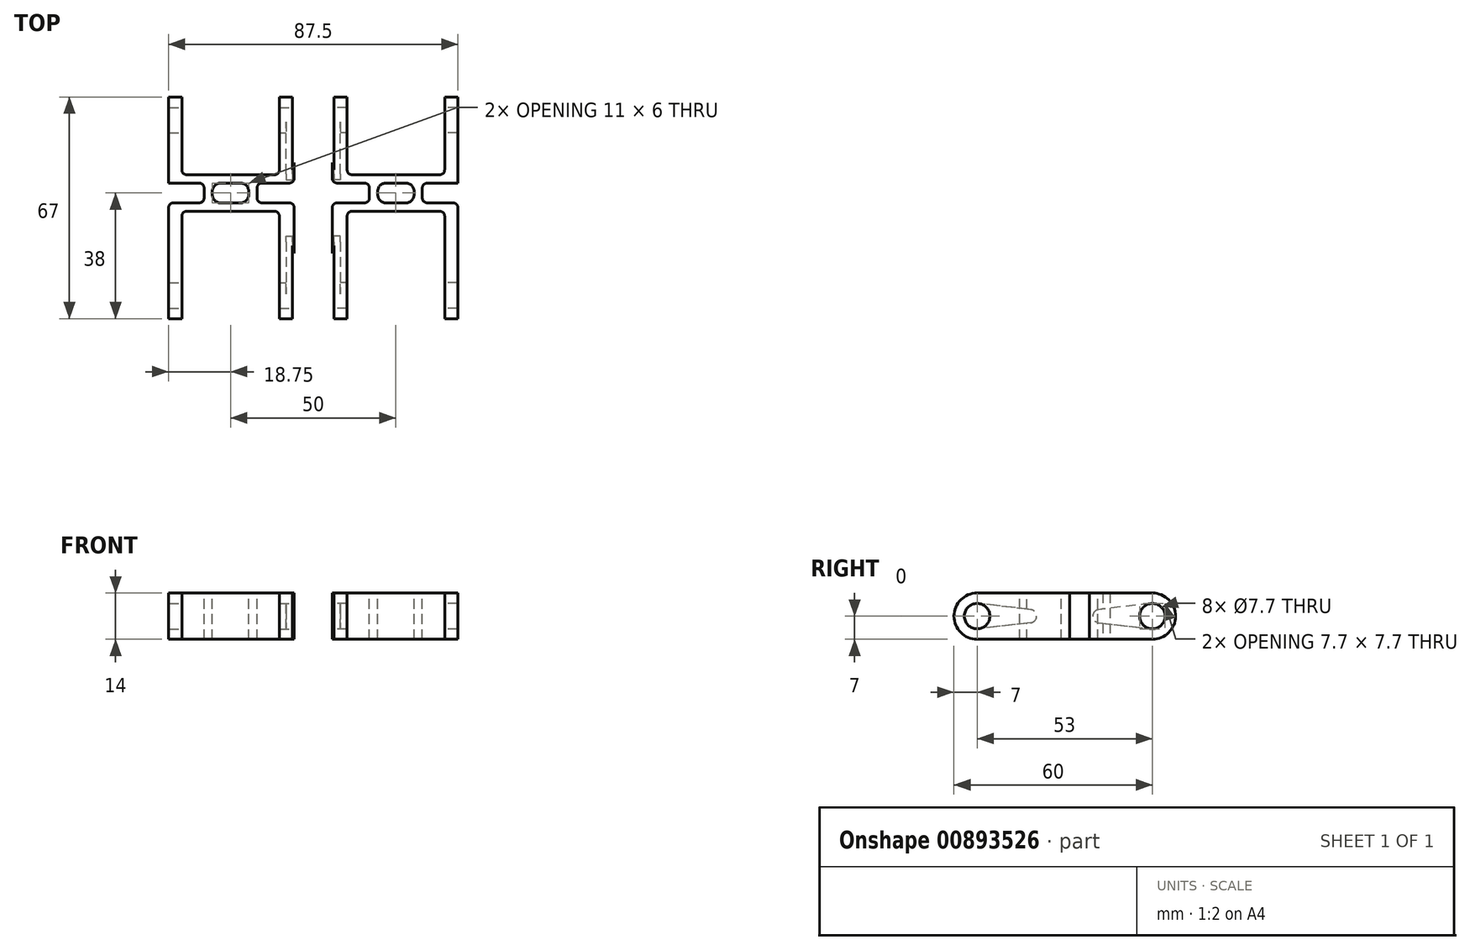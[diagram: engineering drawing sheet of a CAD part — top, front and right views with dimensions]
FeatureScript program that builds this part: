
annotation { "Feature Type Name" : "Feature", "Feature Type Description" : "" }
export const myFeature = defineFeature(function(context is Context, id is Id, definition is map)
    precondition{}
    {
        {
            var Q0;
            Q0=qCreatedBy(makeId("Top.planeOp"),FACE);
            var sketch = newSketch(context, id + "F0", { "sketchPlane" : qUnion([Q0])});
            skLineSegment(sketch, "E0.bottom", {"start": v(18.75, 33.5) * mm, "end": v(-18.75, 33.5) * mm});
            skLineSegment(sketch, "E0.top", {"start": v(18.75, -33.5) * mm, "end": v(-18.75, -33.5) * mm});
            skLineSegment(sketch, "E0.left", {"start": v(18.75, 33.5) * mm, "end": v(18.75, -33.5) * mm});
            skLineSegment(sketch, "E0.right", {"start": v(-18.75, 33.5) * mm, "end": v(-18.75, -33.5) * mm});
            skPoint(sketch, "E0.middle", {"position": v(0, 0) * mm});
            skSolve(sketch);
        }
        {
            var Q0;
            Q0 = qSketchRegion(id + "F0", true);
            extrude(context, id + "F1", {"entities" : qUnion([Q0]), "depth" : 14 * mm, "offsetDistance" : 25 * mm});
        }
        {
            var Q0;
            Q0=makeQuery(id+"F1.opExtrude","CAP_FACE",FACE,{"disambiguationData":[OSD([sQuery(id+"F0.wireOp",EDGE,"E0.bottom"),sQuery(id+"F0.wireOp",EDGE,"E0.top"),sQuery(id+"F0.wireOp",EDGE,"E0.left"),sQuery(id+"F0.wireOp",EDGE,"E0.right")])],"isStart":false});
            var sketch = newSketch(context, id + "F2", { "sketchPlane" : qUnion([Q0])});
            skLineSegment(sketch, "E1.bottom", {"start": v(-18.75, 7.5) * mm, "end": v(-8, 7.5) * mm});
            skLineSegment(sketch, "E1.top", {"start": v(-18.75, 1.5) * mm, "end": v(-8, 1.5) * mm});
            skLineSegment(sketch, "E1.left", {"start": v(-18.75, 7.5) * mm, "end": v(-18.75, 1.5) * mm});
            skLineSegment(sketch, "E1.right", {"start": v(-8, 7.5) * mm, "end": v(-8, 1.5) * mm});
            skLineSegment(sketch, "E2.bottom", {"start": v(18.75, 7.5) * mm, "end": v(8, 7.5) * mm});
            skLineSegment(sketch, "E2.top", {"start": v(18.75, 1.5) * mm, "end": v(8, 1.5) * mm});
            skLineSegment(sketch, "E2.left", {"start": v(18.75, 7.5) * mm, "end": v(18.75, 1.5) * mm});
            skLineSegment(sketch, "E2.right", {"start": v(8, 7.5) * mm, "end": v(8, 1.5) * mm});
            skLineSegment(sketch, "E3.bottom", {"start": v(-14.75, 33.5) * mm, "end": v(14.75, 33.5) * mm});
            skLineSegment(sketch, "E3.top", {"start": v(-14.75, 10) * mm, "end": v(14.75, 10) * mm});
            skLineSegment(sketch, "E3.left", {"start": v(-14.75, 33.5) * mm, "end": v(-14.75, 10) * mm});
            skLineSegment(sketch, "E3.right", {"start": v(14.75, 33.5) * mm, "end": v(14.75, 10) * mm});
            skLineSegment(sketch, "E4.bottom", {"start": v(14.75, -33.5) * mm, "end": v(-14.75, -33.5) * mm});
            skLineSegment(sketch, "E4.top", {"start": v(14.75, -1) * mm, "end": v(-14.75, -1) * mm});
            skLineSegment(sketch, "E4.left", {"start": v(14.75, -33.5) * mm, "end": v(14.75, -1) * mm});
            skLineSegment(sketch, "E4.right", {"start": v(-14.75, -33.5) * mm, "end": v(-14.75, -1) * mm});
            skLineSegment(sketch, "E5", {"start": v(-14.75, 33.5) * mm, "end": v(-18.75, 33.5) * mm, "construction": true});
            skLineSegment(sketch, "E6", {"start": v(14.75, 33.5) * mm, "end": v(18.75, 33.5) * mm, "construction": true});
            skLineSegment(sketch, "E7", {"start": v(18.75, -33.5) * mm, "end": v(14.75, -33.5) * mm, "construction": true});
            skLineSegment(sketch, "E8", {"start": v(-14.75, -33.5) * mm, "end": v(-18.75, -33.5) * mm, "construction": true});
            skSolve(sketch);
        }
        {
            var Q0;
            Q0 = qSketchRegion(id + "F2", true);
            extrude(context, id + "F3", {"entities" : qUnion([Q0]), "operationType" : NewBodyOperationType.REMOVE, "oppositeDirection" : true, "depth" : 25 * mm, "offsetDistance" : 25 * mm});
        }
        {
            var Q0;
            {var subQ0=sQuery(id+"F0.wireOp",EDGE,"E0.right");var subQ1=sQuery(id+"F0.wireOp",EDGE,"E0.top");Q0=makeQuery(id+"F3.boolean.opBoolean","SPLIT",EDGE,{"disambiguationData":[TD([makeQuery(id+"F1.opExtrude","SWEPT_FACE",FACE,{"disambiguationData":[OSD([subQ0])]})])],"derivedFrom":makeQuery(id+"F1.opExtrude","CAP_EDGE",EDGE,{"disambiguationData":[OSD([subQ1])],"isStart":false})});}
            var Q1;
            {var subQ0=sQuery(id+"F0.wireOp",EDGE,"E0.right");var subQ1=sQuery(id+"F0.wireOp",EDGE,"E0.top");Q1=makeQuery(id+"F3.boolean.opBoolean","SPLIT",EDGE,{"disambiguationData":[TD([makeQuery(id+"F1.opExtrude","SWEPT_FACE",FACE,{"disambiguationData":[OSD([subQ0])]})])],"derivedFrom":makeQuery(id+"F1.opExtrude","CAP_EDGE",EDGE,{"disambiguationData":[OSD([subQ1])],"isStart":true})});}
            var Q2;
            {var subQ0=sQuery(id+"F0.wireOp",EDGE,"E0.left");var subQ1=sQuery(id+"F0.wireOp",EDGE,"E0.top");Q2=makeQuery(id+"F3.boolean.opBoolean","SPLIT",EDGE,{"disambiguationData":[TD([makeQuery(id+"F1.opExtrude","SWEPT_FACE",FACE,{"disambiguationData":[OSD([subQ0])]})])],"derivedFrom":makeQuery(id+"F1.opExtrude","CAP_EDGE",EDGE,{"disambiguationData":[OSD([subQ1])],"isStart":false})});}
            var Q3;
            {var subQ0=sQuery(id+"F0.wireOp",EDGE,"E0.left");var subQ1=sQuery(id+"F0.wireOp",EDGE,"E0.top");Q3=makeQuery(id+"F3.boolean.opBoolean","SPLIT",EDGE,{"disambiguationData":[TD([makeQuery(id+"F1.opExtrude","SWEPT_FACE",FACE,{"disambiguationData":[OSD([subQ0])]})])],"derivedFrom":makeQuery(id+"F1.opExtrude","CAP_EDGE",EDGE,{"disambiguationData":[OSD([subQ1])],"isStart":true})});}
            var Q4;
            {var subQ0=sQuery(id+"F0.wireOp",EDGE,"E0.bottom");var subQ1=sQuery(id+"F0.wireOp",EDGE,"E0.right");Q4=makeQuery(id+"F3.boolean.opBoolean","SPLIT",EDGE,{"disambiguationData":[TD([makeQuery(id+"F1.opExtrude","SWEPT_FACE",FACE,{"disambiguationData":[OSD([subQ1])]})])],"derivedFrom":makeQuery(id+"F1.opExtrude","CAP_EDGE",EDGE,{"disambiguationData":[OSD([subQ0])],"isStart":false})});}
            var Q5;
            {var subQ0=sQuery(id+"F0.wireOp",EDGE,"E0.bottom");var subQ1=sQuery(id+"F0.wireOp",EDGE,"E0.left");Q5=makeQuery(id+"F3.boolean.opBoolean","SPLIT",EDGE,{"disambiguationData":[TD([makeQuery(id+"F1.opExtrude","SWEPT_FACE",FACE,{"disambiguationData":[OSD([subQ1])]})])],"derivedFrom":makeQuery(id+"F1.opExtrude","CAP_EDGE",EDGE,{"disambiguationData":[OSD([subQ0])],"isStart":false})});}
            var Q6;
            {var subQ0=sQuery(id+"F0.wireOp",EDGE,"E0.bottom");var subQ1=sQuery(id+"F0.wireOp",EDGE,"E0.right");Q6=makeQuery(id+"F3.boolean.opBoolean","SPLIT",EDGE,{"disambiguationData":[TD([makeQuery(id+"F1.opExtrude","SWEPT_FACE",FACE,{"disambiguationData":[OSD([subQ1])]})])],"derivedFrom":makeQuery(id+"F1.opExtrude","CAP_EDGE",EDGE,{"disambiguationData":[OSD([subQ0])],"isStart":true})});}
            var Q7;
            {var subQ0=sQuery(id+"F0.wireOp",EDGE,"E0.bottom");var subQ1=sQuery(id+"F0.wireOp",EDGE,"E0.left");Q7=makeQuery(id+"F3.boolean.opBoolean","SPLIT",EDGE,{"disambiguationData":[TD([makeQuery(id+"F1.opExtrude","SWEPT_FACE",FACE,{"disambiguationData":[OSD([subQ1])]})])],"derivedFrom":makeQuery(id+"F1.opExtrude","CAP_EDGE",EDGE,{"disambiguationData":[OSD([subQ0])],"isStart":true})});}
            fillet(context, id + "F4", {"entities" : qUnion([Q0, Q1, Q2, Q3, Q4, Q5, Q6, Q7]), "radius" : 7 * mm, "tangentPropagation" : true, "defaultsChanged" : true, "vertexSettings" : [], "allowEdgeOverflow" : false});
        }
        {
            var Q0;
            {var subQ1=sQuery(id+"F0.wireOp",EDGE,"E0.left");var subQ2=sQuery(id+"F0.wireOp",EDGE,"E0.top");Q0=makeQuery(id+"F3.boolean.opBoolean","SPLIT",FACE,{"disambiguationData":[TD([makeQuery(id+"F1.opExtrude","SWEPT_FACE",FACE,{"disambiguationData":[OSD([subQ2])]})])],"derivedFrom":makeQuery(id+"F1.opExtrude","SWEPT_FACE",FACE,{"disambiguationData":[OSD([subQ1])]})});}
            var sketch = newSketch(context, id + "F5", { "sketchPlane" : qUnion([Q0])});
            skCircle(sketch, "E9", {"center": v(-26.5, 7) * mm, "radius": 3.85 * mm});
            skCircle(sketch, "E10", {"center": v(26.5, 7) * mm, "radius": 3.85 * mm});
            skSolve(sketch);
        }
        {
            var Q0;
            Q0 = qSketchRegion(id + "F5", true);
            extrude(context, id + "F6", {"entities" : qUnion([Q0]), "operationType" : NewBodyOperationType.REMOVE, "endBound" : BoundingType.THROUGH_ALL, "oppositeDirection" : true, "depth" : 25 * mm, "offsetDistance" : 25 * mm});
        }
        {
            var Q0;
            {var subQ1=sQuery(id+"F0.wireOp",EDGE,"E0.left");var subQ2=sQuery(id+"F0.wireOp",EDGE,"E0.top");Q0=makeQuery(id+"F3.boolean.opBoolean","SPLIT",FACE,{"disambiguationData":[TD([makeQuery(id+"F1.opExtrude","SWEPT_FACE",FACE,{"disambiguationData":[OSD([subQ2])]})])],"derivedFrom":makeQuery(id+"F1.opExtrude","SWEPT_FACE",FACE,{"disambiguationData":[OSD([subQ1])]})});}
            var sketch = newSketch(context, id + "F7", { "sketchPlane" : qUnion([Q0])});
            skLineSegment(sketch, "E11", {"start": v(-26.5, 7) * mm, "end": v(-10.5, 7) * mm, "construction": true});
            skCircle(sketch, "E12", {"center": v(-10.5, 7) * mm, "radius": 2 * mm});
            skLineSegment(sketch, "E13", {"start": v(26.5, 7) * mm, "end": v(10.5, 7) * mm, "construction": true});
            skCircle(sketch, "E14", {"center": v(10.5, 7) * mm, "radius": 2 * mm});
            skCircle(sketch, "E15.0", {"center": v(-26.5, 7) * mm, "radius": 3.85 * mm});
            skCircle(sketch, "E15.1", {"center": v(26.5, 7) * mm, "radius": 3.85 * mm});
            skLineSegment(sketch, "E16", {"start": v(26.05, 10.82) * mm, "end": v(10.27, 8.99) * mm});
            skLineSegment(sketch, "E17", {"start": v(10.27, 5.01) * mm, "end": v(26.05, 3.18) * mm});
            skLineSegment(sketch, "E18", {"start": v(-10.27, 8.99) * mm, "end": v(-26.05, 10.82) * mm});
            skLineSegment(sketch, "E19", {"start": v(-10.27, 5.01) * mm, "end": v(-26.05, 3.18) * mm});
            skSolve(sketch);
        }
        {
            var Q0;
            {var subQ0=sQuery(id+"F7.wireOp",EDGE,"E18");Q0=makeQuery(id+"F7.imprint","IMPRINT",FACE,{"disambiguationData":[TD([[makeQuery(id+"F7.imprint","IMPRINT",EDGE,{"derivedFrom":subQ0}),1.0]])]});}
            var Q1;
            {var subQ0=sQuery(id+"F7.wireOp",EDGE,"E12");var subQ1=makeQuery(id+"F7.imprint","INTERSECT",VERTEX,{"derivedFrom":[subQ0,sQuery(id+"F7.wireOp",EDGE,"E18")]});Q1=makeQuery(id+"F7.imprint","IMPRINT",FACE,{"disambiguationData":[TD([[makeQuery(id+"F7.imprint","IMPRINT",EDGE,{"disambiguationData":[TD([[subQ1,-1.0]])],"derivedFrom":subQ0}),1.0]])]});}
            var Q2;
            {var subQ0=sQuery(id+"F7.wireOp",EDGE,"E14");var subQ1=makeQuery(id+"F7.imprint","INTERSECT",VERTEX,{"derivedFrom":[subQ0,sQuery(id+"F7.wireOp",EDGE,"E16")]});Q2=makeQuery(id+"F7.imprint","IMPRINT",FACE,{"disambiguationData":[TD([[makeQuery(id+"F7.imprint","IMPRINT",EDGE,{"disambiguationData":[TD([[subQ1,-1.0]])],"derivedFrom":subQ0}),1.0]])]});}
            var Q3;
            {var subQ0=sQuery(id+"F7.wireOp",EDGE,"E16");Q3=makeQuery(id+"F7.imprint","IMPRINT",FACE,{"disambiguationData":[TD([[makeQuery(id+"F7.imprint","IMPRINT",EDGE,{"derivedFrom":subQ0}),1.0]])]});}
            extrude(context, id + "F8", {"entities" : qUnion([Q0, Q1, Q2, Q3]), "operationType" : NewBodyOperationType.REMOVE, "oppositeDirection" : true, "depth" : 1.9 * mm, "offsetDistance" : 25 * mm});
        }
        {
            var Q0;
            Q0=qCreatedBy(makeId("Right.planeOp"),FACE);
            cPlane(context, id + "F9", {"entities" : qUnion([Q0]), "cplaneType" : CPlaneType.OFFSET, "offset" : 25 * mm, "width" : 150 * mm, "height" : 150 * mm});
        }
        {
            var Q0;
            Q0=makeQuery(id+"F1.opExtrude","SWEPT_BODY",BODY,{"disambiguationData":[OSD([sQuery(id+"F0.wireOp",EDGE,"E0.bottom"),sQuery(id+"F0.wireOp",EDGE,"E0.top"),sQuery(id+"F0.wireOp",EDGE,"E0.left"),sQuery(id+"F0.wireOp",EDGE,"E0.right")])]});
            var Q1;
            Q1=qCreatedBy(id+"F9.planeOp",FACE);
            mirror(context, id + "F10", {"entities" : qUnion([Q0]), "mirrorPlane" : qUnion([Q1])});
        }
        {
            var Q0;
            {var subQ1=sQuery(id+"F0.wireOp",EDGE,"E0.left");var subQ2=sQuery(id+"F0.wireOp",EDGE,"E0.top");Q0=makeQuery(id+"F3.boolean.opBoolean","SPLIT",FACE,{"disambiguationData":[TD([makeQuery(id+"F1.opExtrude","SWEPT_FACE",FACE,{"disambiguationData":[OSD([subQ2])]})])],"derivedFrom":makeQuery(id+"F1.opExtrude","SWEPT_FACE",FACE,{"disambiguationData":[OSD([subQ1])]})});}
            var Q1;
            {var subQ1=sQuery(id+"F0.wireOp",EDGE,"E0.left");var subQ2=sQuery(id+"F0.wireOp",EDGE,"E0.top");Q1=makeQuery(id+"F3.boolean.opBoolean","SPLIT",FACE,{"disambiguationData":[TD([makeQuery(id+"F1.opExtrude","SWEPT_FACE",FACE,{"disambiguationData":[OSD([subQ2])]})])],"derivedFrom":makeQuery(id+"F1.opExtrude","SWEPT_FACE",FACE,{"disambiguationData":[OSD([subQ1])]})});}
            var sketch = newSketch(context, id + "F11", { "sketchPlane" : qUnion([Q0, Q1])});
            skLineSegment(sketch, "E20.bottom", {"start": v(-16.5, 14) * mm, "end": v(1.5, 14) * mm});
            skLineSegment(sketch, "E20.top", {"start": v(-16.5, 0) * mm, "end": v(1.5, 0) * mm});
            skLineSegment(sketch, "E20.left", {"start": v(-16.5, 14) * mm, "end": v(-16.5, 0) * mm});
            skLineSegment(sketch, "E20.right", {"start": v(1.5, 14) * mm, "end": v(1.5, 0) * mm});
            skLineSegment(sketch, "E21.bottom", {"start": v(7.5, 0) * mm, "end": v(16.5, 0) * mm});
            skLineSegment(sketch, "E21.top", {"start": v(7.5, 14) * mm, "end": v(16.5, 14) * mm});
            skLineSegment(sketch, "E21.left", {"start": v(7.5, 0) * mm, "end": v(7.5, 14) * mm});
            skLineSegment(sketch, "E21.right", {"start": v(16.5, 0) * mm, "end": v(16.5, 14) * mm});
            skSolve(sketch);
        }
        {
            var Q0;
            Q0 = qSketchRegion(id + "F11", true);
            extrude(context, id + "F12", {"entities" : qUnion([Q0]), "operationType" : NewBodyOperationType.ADD, "depth" : 0.5 * mm, "offsetDistance" : 25 * mm});
        }
        {
            var Q0;
            {var subQ1=sQuery(id+"F0.wireOp",EDGE,"E0.left");var subQ2=sQuery(id+"F0.wireOp",EDGE,"E0.top");Q0=makeQuery(id+"F10.opPattern","COPY",FACE,{"derivedFrom":makeQuery(id+"F3.boolean.opBoolean","SPLIT",FACE,{"disambiguationData":[TD([makeQuery(id+"F1.opExtrude","SWEPT_FACE",FACE,{"disambiguationData":[OSD([subQ2])]})])],"derivedFrom":makeQuery(id+"F1.opExtrude","SWEPT_FACE",FACE,{"disambiguationData":[OSD([subQ1])]})}),"instanceName":"1"});}
            var sketch = newSketch(context, id + "F13", { "sketchPlane" : qUnion([Q0])});
            skLineSegment(sketch, "E22.bottom", {"start": v(-1.5, 14) * mm, "end": v(16.5, 14) * mm});
            skLineSegment(sketch, "E22.top", {"start": v(-1.5, 0) * mm, "end": v(16.5, 0) * mm});
            skLineSegment(sketch, "E22.left", {"start": v(-1.5, 14) * mm, "end": v(-1.5, 0) * mm});
            skLineSegment(sketch, "E22.right", {"start": v(16.5, 14) * mm, "end": v(16.5, 0) * mm});
            skLineSegment(sketch, "E23.bottom", {"start": v(-7.5, 14) * mm, "end": v(-16.5, 14) * mm});
            skLineSegment(sketch, "E23.top", {"start": v(-7.5, 0) * mm, "end": v(-16.5, 0) * mm});
            skLineSegment(sketch, "E23.left", {"start": v(-7.5, 14) * mm, "end": v(-7.5, 0) * mm});
            skLineSegment(sketch, "E23.right", {"start": v(-16.5, 14) * mm, "end": v(-16.5, 0) * mm});
            skSolve(sketch);
        }
        {
            var Q0;
            Q0 = qSketchRegion(id + "F13", true);
            extrude(context, id + "F14", {"entities" : qUnion([Q0]), "operationType" : NewBodyOperationType.ADD, "depth" : 0.5 * mm, "offsetDistance" : 25 * mm});
        }
        {
            var Q0;
            Q0=makeQuery(id+"F12.opExtrude","CAP_EDGE",EDGE,{"disambiguationData":[OSD([sQuery(id+"F11.wireOp",EDGE,"E20.right")])],"isStart":false});
            var Q1;
            Q1=makeQuery(id+"F12.opExtrude","CAP_EDGE",EDGE,{"disambiguationData":[OSD([sQuery(id+"F11.wireOp",EDGE,"E21.left")])],"isStart":false});
            var Q2;
            Q2=makeQuery(id+"F3.boolean.opBoolean","COPY",EDGE,{"derivedFrom":makeQuery(id+"F3.opExtrude","SWEPT_EDGE",EDGE,{"disambiguationData":[OSD([sQuery(id+"F2.wireOp",EDGE,"E2.bottom"),sQuery(id+"F2.wireOp",EDGE,"E2.right")])]})});
            var Q3;
            Q3=makeQuery(id+"F3.boolean.opBoolean","COPY",EDGE,{"derivedFrom":makeQuery(id+"F3.opExtrude","SWEPT_EDGE",EDGE,{"disambiguationData":[OSD([sQuery(id+"F2.wireOp",EDGE,"E2.top"),sQuery(id+"F2.wireOp",EDGE,"E2.right")])]})});
            var Q4;
            Q4=makeQuery(id+"F3.boolean.opBoolean","COPY",EDGE,{"derivedFrom":makeQuery(id+"F3.opExtrude","SWEPT_EDGE",EDGE,{"disambiguationData":[OSD([sQuery(id+"F0.wireOp",EDGE,"E0.right"),sQuery(id+"F2.wireOp",EDGE,"E1.bottom"),sQuery(id+"F2.wireOp",EDGE,"E1.left")])]})});
            var Q5;
            Q5=makeQuery(id+"F3.boolean.opBoolean","COPY",EDGE,{"derivedFrom":makeQuery(id+"F3.opExtrude","SWEPT_EDGE",EDGE,{"disambiguationData":[OSD([sQuery(id+"F0.wireOp",EDGE,"E0.right"),sQuery(id+"F2.wireOp",EDGE,"E1.top"),sQuery(id+"F2.wireOp",EDGE,"E1.left")])]})});
            var Q6;
            Q6=makeQuery(id+"F3.boolean.opBoolean","COPY",EDGE,{"derivedFrom":makeQuery(id+"F3.opExtrude","SWEPT_EDGE",EDGE,{"disambiguationData":[OSD([sQuery(id+"F2.wireOp",EDGE,"E1.bottom"),sQuery(id+"F2.wireOp",EDGE,"E1.right")])]})});
            var Q7;
            Q7=makeQuery(id+"F3.boolean.opBoolean","COPY",EDGE,{"derivedFrom":makeQuery(id+"F3.opExtrude","SWEPT_EDGE",EDGE,{"disambiguationData":[OSD([sQuery(id+"F2.wireOp",EDGE,"E1.top"),sQuery(id+"F2.wireOp",EDGE,"E1.right")])]})});
            var Q8;
            Q8=makeQuery(id+"F3.boolean.opBoolean","COPY",EDGE,{"derivedFrom":makeQuery(id+"F3.opExtrude","SWEPT_EDGE",EDGE,{"disambiguationData":[OSD([sQuery(id+"F2.wireOp",EDGE,"E4.top"),sQuery(id+"F2.wireOp",EDGE,"E4.right")])]})});
            var Q9;
            Q9=makeQuery(id+"F3.boolean.opBoolean","COPY",EDGE,{"derivedFrom":makeQuery(id+"F3.opExtrude","SWEPT_EDGE",EDGE,{"disambiguationData":[OSD([sQuery(id+"F2.wireOp",EDGE,"E4.top"),sQuery(id+"F2.wireOp",EDGE,"E4.left")])]})});
            var Q10;
            Q10=makeQuery(id+"F3.boolean.opBoolean","COPY",EDGE,{"derivedFrom":makeQuery(id+"F3.opExtrude","SWEPT_EDGE",EDGE,{"disambiguationData":[OSD([sQuery(id+"F2.wireOp",EDGE,"E3.top"),sQuery(id+"F2.wireOp",EDGE,"E3.left")])]})});
            var Q11;
            Q11=makeQuery(id+"F3.boolean.opBoolean","COPY",EDGE,{"derivedFrom":makeQuery(id+"F3.opExtrude","SWEPT_EDGE",EDGE,{"disambiguationData":[OSD([sQuery(id+"F2.wireOp",EDGE,"E3.top"),sQuery(id+"F2.wireOp",EDGE,"E3.right")])]})});
            var Q12;
            Q12=makeQuery(id+"F14.opExtrude","CAP_EDGE",EDGE,{"disambiguationData":[OSD([sQuery(id+"F13.wireOp",EDGE,"E23.left")])],"isStart":false});
            var Q13;
            Q13=makeQuery(id+"F14.opExtrude","CAP_EDGE",EDGE,{"disambiguationData":[OSD([sQuery(id+"F13.wireOp",EDGE,"E22.left")])],"isStart":false});
            var Q14;
            Q14=makeQuery(id+"F10.opPattern","COPY",EDGE,{"derivedFrom":makeQuery(id+"F3.boolean.opBoolean","COPY",EDGE,{"derivedFrom":makeQuery(id+"F3.opExtrude","SWEPT_EDGE",EDGE,{"disambiguationData":[OSD([sQuery(id+"F2.wireOp",EDGE,"E2.top"),sQuery(id+"F2.wireOp",EDGE,"E2.right")])]})}),"instanceName":"1"});
            var Q15;
            Q15=makeQuery(id+"F10.opPattern","COPY",EDGE,{"derivedFrom":makeQuery(id+"F3.boolean.opBoolean","COPY",EDGE,{"derivedFrom":makeQuery(id+"F3.opExtrude","SWEPT_EDGE",EDGE,{"disambiguationData":[OSD([sQuery(id+"F2.wireOp",EDGE,"E2.bottom"),sQuery(id+"F2.wireOp",EDGE,"E2.right")])]})}),"instanceName":"1"});
            var Q16;
            Q16=makeQuery(id+"F10.opPattern","COPY",EDGE,{"derivedFrom":makeQuery(id+"F3.boolean.opBoolean","COPY",EDGE,{"derivedFrom":makeQuery(id+"F3.opExtrude","SWEPT_EDGE",EDGE,{"disambiguationData":[OSD([sQuery(id+"F2.wireOp",EDGE,"E1.bottom"),sQuery(id+"F2.wireOp",EDGE,"E1.right")])]})}),"instanceName":"1"});
            var Q17;
            Q17=makeQuery(id+"F10.opPattern","COPY",EDGE,{"derivedFrom":makeQuery(id+"F3.boolean.opBoolean","COPY",EDGE,{"derivedFrom":makeQuery(id+"F3.opExtrude","SWEPT_EDGE",EDGE,{"disambiguationData":[OSD([sQuery(id+"F0.wireOp",EDGE,"E0.right"),sQuery(id+"F2.wireOp",EDGE,"E1.bottom"),sQuery(id+"F2.wireOp",EDGE,"E1.left")])]})}),"instanceName":"1"});
            var Q18;
            Q18=makeQuery(id+"F10.opPattern","COPY",EDGE,{"derivedFrom":makeQuery(id+"F3.boolean.opBoolean","COPY",EDGE,{"derivedFrom":makeQuery(id+"F3.opExtrude","SWEPT_EDGE",EDGE,{"disambiguationData":[OSD([sQuery(id+"F0.wireOp",EDGE,"E0.right"),sQuery(id+"F2.wireOp",EDGE,"E1.top"),sQuery(id+"F2.wireOp",EDGE,"E1.left")])]})}),"instanceName":"1"});
            var Q19;
            Q19=makeQuery(id+"F10.opPattern","COPY",EDGE,{"derivedFrom":makeQuery(id+"F3.boolean.opBoolean","COPY",EDGE,{"derivedFrom":makeQuery(id+"F3.opExtrude","SWEPT_EDGE",EDGE,{"disambiguationData":[OSD([sQuery(id+"F2.wireOp",EDGE,"E1.top"),sQuery(id+"F2.wireOp",EDGE,"E1.right")])]})}),"instanceName":"1"});
            var Q20;
            Q20=makeQuery(id+"F10.opPattern","COPY",EDGE,{"derivedFrom":makeQuery(id+"F3.boolean.opBoolean","COPY",EDGE,{"derivedFrom":makeQuery(id+"F3.opExtrude","SWEPT_EDGE",EDGE,{"disambiguationData":[OSD([sQuery(id+"F2.wireOp",EDGE,"E3.top"),sQuery(id+"F2.wireOp",EDGE,"E3.right")])]})}),"instanceName":"1"});
            var Q21;
            Q21=makeQuery(id+"F10.opPattern","COPY",EDGE,{"derivedFrom":makeQuery(id+"F3.boolean.opBoolean","COPY",EDGE,{"derivedFrom":makeQuery(id+"F3.opExtrude","SWEPT_EDGE",EDGE,{"disambiguationData":[OSD([sQuery(id+"F2.wireOp",EDGE,"E4.top"),sQuery(id+"F2.wireOp",EDGE,"E4.left")])]})}),"instanceName":"1"});
            var Q22;
            Q22=makeQuery(id+"F10.opPattern","COPY",EDGE,{"derivedFrom":makeQuery(id+"F3.boolean.opBoolean","COPY",EDGE,{"derivedFrom":makeQuery(id+"F3.opExtrude","SWEPT_EDGE",EDGE,{"disambiguationData":[OSD([sQuery(id+"F2.wireOp",EDGE,"E3.top"),sQuery(id+"F2.wireOp",EDGE,"E3.left")])]})}),"instanceName":"1"});
            var Q23;
            Q23=makeQuery(id+"F10.opPattern","COPY",EDGE,{"derivedFrom":makeQuery(id+"F3.boolean.opBoolean","COPY",EDGE,{"derivedFrom":makeQuery(id+"F3.opExtrude","SWEPT_EDGE",EDGE,{"disambiguationData":[OSD([sQuery(id+"F2.wireOp",EDGE,"E4.top"),sQuery(id+"F2.wireOp",EDGE,"E4.right")])]})}),"instanceName":"1"});
            fillet(context, id + "F15", {"entities" : qUnion([Q0, Q1, Q2, Q3, Q4, Q5, Q6, Q7, Q8, Q9, Q10, Q11, Q12, Q13, Q14, Q15, Q16, Q17, Q18, Q19, Q20, Q21, Q22, Q23]), "radius" : 1.5 * mm, "tangentPropagation" : true, "defaultsChanged" : true, "vertexSettings" : [], "allowEdgeOverflow" : false});
        }
        {
            var Q0;
            Q0=makeQuery(id+"F12.boolean.opBoolean","MERGE",FACE,{"derivedFrom":[makeQuery(id+"F1.opExtrude","CAP_FACE",FACE,{"disambiguationData":[OSD([sQuery(id+"F0.wireOp",EDGE,"E0.bottom"),sQuery(id+"F0.wireOp",EDGE,"E0.top"),sQuery(id+"F0.wireOp",EDGE,"E0.left"),sQuery(id+"F0.wireOp",EDGE,"E0.right")])],"isStart":false}),makeQuery(id+"F12.opExtrude","SWEPT_FACE",FACE,{"disambiguationData":[OSD([sQuery(id+"F11.wireOp",EDGE,"E20.bottom")])]}),makeQuery(id+"F12.opExtrude","SWEPT_FACE",FACE,{"disambiguationData":[OSD([sQuery(id+"F11.wireOp",EDGE,"E21.top")])]})]});
            var sketch = newSketch(context, id + "F16", { "sketchPlane" : qUnion([Q0])});
            skLineSegment(sketch, "E24", {"start": v(-8, 4.5) * mm, "end": v(8, 4.5) * mm, "construction": true});
            skLineSegment(sketch, "E25", {"start": v(42, 4.5) * mm, "end": v(58, 4.5) * mm, "construction": true});
            skLineSegment(sketch, "E26.bottom", {"start": v(5.5, 1.5) * mm, "end": v(-5.5, 1.5) * mm});
            skLineSegment(sketch, "E26.top", {"start": v(5.5, 7.5) * mm, "end": v(-5.5, 7.5) * mm});
            skLineSegment(sketch, "E26.left", {"start": v(5.5, 1.5) * mm, "end": v(5.5, 7.5) * mm});
            skLineSegment(sketch, "E26.right", {"start": v(-5.5, 1.5) * mm, "end": v(-5.5, 7.5) * mm});
            skPoint(sketch, "E26.middle", {"position": v(0, 4.5) * mm});
            skLineSegment(sketch, "E27.bottom", {"start": v(44.5, 1.5) * mm, "end": v(55.5, 1.5) * mm});
            skLineSegment(sketch, "E27.top", {"start": v(44.5, 7.5) * mm, "end": v(55.5, 7.5) * mm});
            skLineSegment(sketch, "E27.left", {"start": v(44.5, 1.5) * mm, "end": v(44.5, 7.5) * mm});
            skLineSegment(sketch, "E27.right", {"start": v(55.5, 1.5) * mm, "end": v(55.5, 7.5) * mm});
            skPoint(sketch, "E27.middle", {"position": v(50, 4.5) * mm});
            skSolve(sketch);
        }
        {
            var Q0;
            Q0 = qSketchRegion(id + "F16", true);
            extrude(context, id + "F17", {"entities" : qUnion([Q0]), "operationType" : NewBodyOperationType.REMOVE, "oppositeDirection" : true, "depth" : 25 * mm, "offsetDistance" : 25 * mm});
        }
        {
            var Q0;
            Q0=makeQuery(id+"F17.boolean.opBoolean","COPY",EDGE,{"derivedFrom":makeQuery(id+"F17.opExtrude","SWEPT_EDGE",EDGE,{"disambiguationData":[OSD([sQuery(id+"F16.wireOp",EDGE,"E26.top"),sQuery(id+"F16.wireOp",EDGE,"E26.right")])]})});
            var Q1;
            Q1=makeQuery(id+"F17.boolean.opBoolean","COPY",EDGE,{"derivedFrom":makeQuery(id+"F17.opExtrude","SWEPT_EDGE",EDGE,{"disambiguationData":[OSD([sQuery(id+"F16.wireOp",EDGE,"E27.top"),sQuery(id+"F16.wireOp",EDGE,"E27.left")])]})});
            var Q2;
            Q2=makeQuery(id+"F17.boolean.opBoolean","COPY",EDGE,{"derivedFrom":makeQuery(id+"F17.opExtrude","SWEPT_EDGE",EDGE,{"disambiguationData":[OSD([sQuery(id+"F16.wireOp",EDGE,"E26.top"),sQuery(id+"F16.wireOp",EDGE,"E26.left")])]})});
            var Q3;
            Q3=makeQuery(id+"F17.boolean.opBoolean","COPY",EDGE,{"derivedFrom":makeQuery(id+"F17.opExtrude","SWEPT_EDGE",EDGE,{"disambiguationData":[OSD([sQuery(id+"F16.wireOp",EDGE,"E27.top"),sQuery(id+"F16.wireOp",EDGE,"E27.right")])]})});
            var Q4;
            Q4=makeQuery(id+"F17.boolean.opBoolean","COPY",EDGE,{"derivedFrom":makeQuery(id+"F17.opExtrude","SWEPT_EDGE",EDGE,{"disambiguationData":[OSD([sQuery(id+"F16.wireOp",EDGE,"E27.bottom"),sQuery(id+"F16.wireOp",EDGE,"E27.right")])]})});
            var Q5;
            Q5=makeQuery(id+"F17.boolean.opBoolean","COPY",EDGE,{"derivedFrom":makeQuery(id+"F17.opExtrude","SWEPT_EDGE",EDGE,{"disambiguationData":[OSD([sQuery(id+"F16.wireOp",EDGE,"E26.bottom"),sQuery(id+"F16.wireOp",EDGE,"E26.left")])]})});
            var Q6;
            Q6=makeQuery(id+"F17.boolean.opBoolean","COPY",EDGE,{"derivedFrom":makeQuery(id+"F17.opExtrude","SWEPT_EDGE",EDGE,{"disambiguationData":[OSD([sQuery(id+"F16.wireOp",EDGE,"E26.bottom"),sQuery(id+"F16.wireOp",EDGE,"E26.right")])]})});
            var Q7;
            Q7=makeQuery(id+"F17.boolean.opBoolean","COPY",EDGE,{"derivedFrom":makeQuery(id+"F17.opExtrude","SWEPT_EDGE",EDGE,{"disambiguationData":[OSD([sQuery(id+"F16.wireOp",EDGE,"E27.bottom"),sQuery(id+"F16.wireOp",EDGE,"E27.left")])]})});
            fillet(context, id + "F18", {"entities" : qUnion([Q0, Q1, Q2, Q3, Q4, Q5, Q6, Q7]), "radius" : 2.5 * mm, "tangentPropagation" : true, "allowEdgeOverflow" : false});
        }
        {
            var Q0;
            {var subQ0=sQuery(id+"F11.wireOp",EDGE,"E21.right");var subQ2=sQuery(id+"F0.wireOp",EDGE,"E0.left");var subQ3=makeQuery(id+"F1.opExtrude","SWEPT_FACE",FACE,{"disambiguationData":[OSD([subQ2])]});var subQ4=makeQuery(id+"F12.opExtrude","SWEPT_FACE",FACE,{"disambiguationData":[OSD([subQ0])]});Q0=makeQuery(id+"F12.boolean.opBoolean","SPLIT",EDGE,{"disambiguationData":[topologyDisambiguationEdgeConnected([subQ3,subQ4]),TD([makeQuery(id+"F8.boolean.opBoolean","COPY",FACE,{"derivedFrom":makeQuery(id+"F8.opExtrude","SWEPT_FACE",FACE,{"disambiguationData":[OSD([sQuery(id+"F7.wireOp",EDGE,"E17")])]})})])],"derivedFrom":makeQuery(id+"F12.opExtrude","CAP_EDGE",EDGE,{"disambiguationData":[OSD([subQ0])],"isStart":true})});}
            var Q1;
            {var subQ0=sQuery(id+"F11.wireOp",EDGE,"E21.right");var subQ1=makeQuery(id+"F12.opExtrude","SWEPT_FACE",FACE,{"disambiguationData":[OSD([subQ0])]});var subQ2=sQuery(id+"F0.wireOp",EDGE,"E0.left");var subQ3=makeQuery(id+"F1.opExtrude","SWEPT_FACE",FACE,{"disambiguationData":[OSD([subQ2])]});Q1=makeQuery(id+"F12.boolean.opBoolean","SPLIT",EDGE,{"disambiguationData":[topologyDisambiguationEdgeConnected([subQ3,subQ1]),TD([makeQuery(id+"F8.boolean.opBoolean","COPY",FACE,{"derivedFrom":makeQuery(id+"F8.opExtrude","SWEPT_FACE",FACE,{"disambiguationData":[OSD([sQuery(id+"F7.wireOp",EDGE,"E16")])]})})])],"derivedFrom":makeQuery(id+"F12.opExtrude","CAP_EDGE",EDGE,{"disambiguationData":[OSD([subQ0])],"isStart":true})});}
            var Q2;
            {var subQ0=sQuery(id+"F0.wireOp",EDGE,"E0.bottom");var subQ2=sQuery(id+"F0.wireOp",EDGE,"E0.left");var subQ5=makeQuery(id+"F10.opPattern","COPY",FACE,{"derivedFrom":makeQuery(id+"F3.boolean.opBoolean","SPLIT",FACE,{"disambiguationData":[TD([makeQuery(id+"F1.opExtrude","SWEPT_FACE",FACE,{"disambiguationData":[OSD([subQ0])]})])],"derivedFrom":makeQuery(id+"F1.opExtrude","SWEPT_FACE",FACE,{"disambiguationData":[OSD([subQ2])]})}),"instanceName":"1"});var subQ6=sQuery(id+"F13.wireOp",EDGE,"E23.right");var subQ8=makeQuery(id+"F14.opExtrude","SWEPT_FACE",FACE,{"disambiguationData":[OSD([subQ6])]});Q2=makeQuery(id+"F14.boolean.opBoolean","SPLIT",EDGE,{"disambiguationData":[topologyDisambiguationEdgeConnected([subQ5,subQ8]),TD([makeQuery(id+"F10.opPattern","COPY",FACE,{"derivedFrom":makeQuery(id+"F8.boolean.opBoolean","COPY",FACE,{"derivedFrom":makeQuery(id+"F8.opExtrude","SWEPT_FACE",FACE,{"disambiguationData":[OSD([sQuery(id+"F7.wireOp",EDGE,"E17")])]})}),"instanceName":"1"})])],"derivedFrom":makeQuery(id+"F14.opExtrude","CAP_EDGE",EDGE,{"disambiguationData":[OSD([subQ6])],"isStart":true})});}
            var Q3;
            {var subQ0=sQuery(id+"F13.wireOp",EDGE,"E23.right");var subQ1=makeQuery(id+"F14.opExtrude","SWEPT_FACE",FACE,{"disambiguationData":[OSD([subQ0])]});var subQ2=sQuery(id+"F0.wireOp",EDGE,"E0.bottom");var subQ4=sQuery(id+"F0.wireOp",EDGE,"E0.left");var subQ7=makeQuery(id+"F10.opPattern","COPY",FACE,{"derivedFrom":makeQuery(id+"F3.boolean.opBoolean","SPLIT",FACE,{"disambiguationData":[TD([makeQuery(id+"F1.opExtrude","SWEPT_FACE",FACE,{"disambiguationData":[OSD([subQ2])]})])],"derivedFrom":makeQuery(id+"F1.opExtrude","SWEPT_FACE",FACE,{"disambiguationData":[OSD([subQ4])]})}),"instanceName":"1"});Q3=makeQuery(id+"F14.boolean.opBoolean","SPLIT",EDGE,{"disambiguationData":[topologyDisambiguationEdgeConnected([subQ7,subQ1]),TD([makeQuery(id+"F10.opPattern","COPY",FACE,{"derivedFrom":makeQuery(id+"F8.boolean.opBoolean","COPY",FACE,{"derivedFrom":makeQuery(id+"F8.opExtrude","SWEPT_FACE",FACE,{"disambiguationData":[OSD([sQuery(id+"F7.wireOp",EDGE,"E16")])]})}),"instanceName":"1"})])],"derivedFrom":makeQuery(id+"F14.opExtrude","CAP_EDGE",EDGE,{"disambiguationData":[OSD([subQ0])],"isStart":true})});}
            var Q4;
            {var subQ0=sQuery(id+"F13.wireOp",EDGE,"E22.right");var subQ3=sQuery(id+"F0.wireOp",EDGE,"E0.left");var subQ4=sQuery(id+"F0.wireOp",EDGE,"E0.top");var subQ7=makeQuery(id+"F10.opPattern","COPY",FACE,{"derivedFrom":makeQuery(id+"F3.boolean.opBoolean","SPLIT",FACE,{"disambiguationData":[TD([makeQuery(id+"F1.opExtrude","SWEPT_FACE",FACE,{"disambiguationData":[OSD([subQ4])]})])],"derivedFrom":makeQuery(id+"F1.opExtrude","SWEPT_FACE",FACE,{"disambiguationData":[OSD([subQ3])]})}),"instanceName":"1"});var subQ8=makeQuery(id+"F14.opExtrude","SWEPT_FACE",FACE,{"disambiguationData":[OSD([subQ0])]});Q4=makeQuery(id+"F14.boolean.opBoolean","SPLIT",EDGE,{"disambiguationData":[topologyDisambiguationEdgeConnected([subQ7,subQ8]),TD([makeQuery(id+"F10.opPattern","COPY",FACE,{"derivedFrom":makeQuery(id+"F8.boolean.opBoolean","COPY",FACE,{"derivedFrom":makeQuery(id+"F8.opExtrude","SWEPT_FACE",FACE,{"disambiguationData":[OSD([sQuery(id+"F7.wireOp",EDGE,"E19")])]})}),"instanceName":"1"})])],"derivedFrom":makeQuery(id+"F14.opExtrude","CAP_EDGE",EDGE,{"disambiguationData":[OSD([subQ0])],"isStart":true})});}
            var Q5;
            {var subQ2=sQuery(id+"F0.wireOp",EDGE,"E0.left");var subQ3=sQuery(id+"F0.wireOp",EDGE,"E0.top");var subQ6=makeQuery(id+"F10.opPattern","COPY",FACE,{"derivedFrom":makeQuery(id+"F3.boolean.opBoolean","SPLIT",FACE,{"disambiguationData":[TD([makeQuery(id+"F1.opExtrude","SWEPT_FACE",FACE,{"disambiguationData":[OSD([subQ3])]})])],"derivedFrom":makeQuery(id+"F1.opExtrude","SWEPT_FACE",FACE,{"disambiguationData":[OSD([subQ2])]})}),"instanceName":"1"});var subQ7=sQuery(id+"F13.wireOp",EDGE,"E22.right");var subQ8=makeQuery(id+"F14.opExtrude","SWEPT_FACE",FACE,{"disambiguationData":[OSD([subQ7])]});Q5=makeQuery(id+"F14.boolean.opBoolean","SPLIT",EDGE,{"disambiguationData":[topologyDisambiguationEdgeConnected([subQ6,subQ8]),TD([makeQuery(id+"F10.opPattern","COPY",FACE,{"derivedFrom":makeQuery(id+"F8.boolean.opBoolean","COPY",FACE,{"derivedFrom":makeQuery(id+"F8.opExtrude","SWEPT_FACE",FACE,{"disambiguationData":[OSD([sQuery(id+"F7.wireOp",EDGE,"E18")])]})}),"instanceName":"1"})])],"derivedFrom":makeQuery(id+"F14.opExtrude","CAP_EDGE",EDGE,{"disambiguationData":[OSD([subQ7])],"isStart":true})});}
            var Q6;
            {var subQ1=sQuery(id+"F0.wireOp",EDGE,"E0.left");var subQ2=makeQuery(id+"F1.opExtrude","SWEPT_FACE",FACE,{"disambiguationData":[OSD([subQ1])]});var subQ3=sQuery(id+"F11.wireOp",EDGE,"E20.left");var subQ4=makeQuery(id+"F12.opExtrude","SWEPT_FACE",FACE,{"disambiguationData":[OSD([subQ3])]});Q6=makeQuery(id+"F12.boolean.opBoolean","SPLIT",EDGE,{"disambiguationData":[topologyDisambiguationEdgeConnected([subQ2,subQ4]),TD([makeQuery(id+"F8.boolean.opBoolean","COPY",FACE,{"derivedFrom":makeQuery(id+"F8.opExtrude","SWEPT_FACE",FACE,{"disambiguationData":[OSD([sQuery(id+"F7.wireOp",EDGE,"E18")])]})})])],"derivedFrom":makeQuery(id+"F12.opExtrude","CAP_EDGE",EDGE,{"disambiguationData":[OSD([subQ3])],"isStart":true})});}
            var Q7;
            {var subQ0=sQuery(id+"F0.wireOp",EDGE,"E0.left");var subQ1=makeQuery(id+"F1.opExtrude","SWEPT_FACE",FACE,{"disambiguationData":[OSD([subQ0])]});var subQ2=sQuery(id+"F11.wireOp",EDGE,"E20.left");var subQ4=makeQuery(id+"F12.opExtrude","SWEPT_FACE",FACE,{"disambiguationData":[OSD([subQ2])]});Q7=makeQuery(id+"F12.boolean.opBoolean","SPLIT",EDGE,{"disambiguationData":[topologyDisambiguationEdgeConnected([subQ1,subQ4]),TD([makeQuery(id+"F8.boolean.opBoolean","COPY",FACE,{"derivedFrom":makeQuery(id+"F8.opExtrude","SWEPT_FACE",FACE,{"disambiguationData":[OSD([sQuery(id+"F7.wireOp",EDGE,"E19")])]})})])],"derivedFrom":makeQuery(id+"F12.opExtrude","CAP_EDGE",EDGE,{"disambiguationData":[OSD([subQ2])],"isStart":true})});}
            fillet(context, id + "F19", {"entities" : qUnion([Q0, Q1, Q2, Q3, Q4, Q5, Q6, Q7]), "radius" : 5 * mm, "tangentPropagation" : true, "allowEdgeOverflow" : false});
        }
    });
